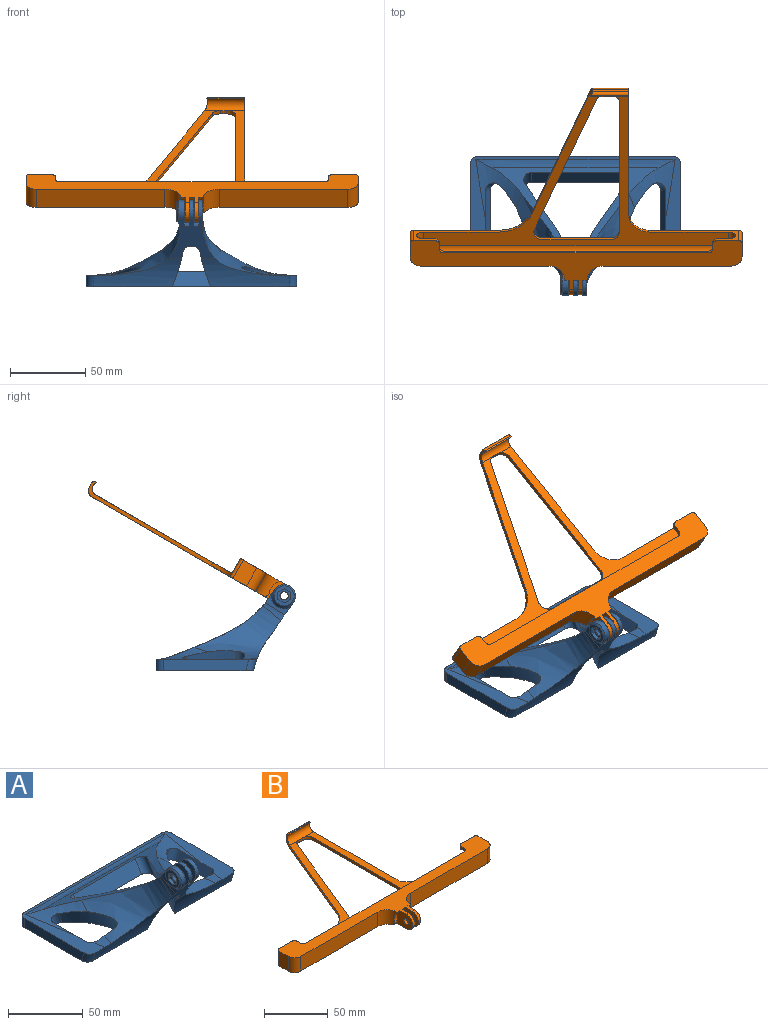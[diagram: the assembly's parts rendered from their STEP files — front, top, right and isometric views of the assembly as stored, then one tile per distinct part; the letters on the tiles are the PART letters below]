
ASSEMBLY  parts=2 mates=1
PART A: 71 faces, bbox 183.3x107.2x68.2 mm
  f0: plane 140.82x67.89mm, normal (0,0,1), area 1387.2mm2, adj f2,f3,f4,f6,f17,f18,f19,f30
  f1: bspline ~80.55x44.88mm, area 1328.5mm2, adj f2,f3,f6,f11,f21,f62,f63,f67
  f2: bspline ~44.93x33.78mm, area 387mm2, adj f0,f1,f21,f55,f63,f64,f65
  f3: bspline ~12.63x10.46mm, area 71.5mm2, adj f0,f1,f6,f66,f67
  f4: bspline ~12.63x10.46mm, area 71.5mm2, adj f0,f20,f30,f58,f59
  f5: plane 142.8x67.8mm, normal (0,0,-1), area 4885.5mm2, adj f6,f17,f18,f19,f30,f38,f39,f40
  f6: cylinder r=49.45mm len=58.6mm, axis (1,0,0), area 654.4mm2, adj f0,f1,f3,f5,f11,f41,f46
  f7: cylinder r=2.75mm len=5.5mm, axis (1,0,0), area 43.2mm2, adj f28,f37
  f8: plane 13.25x13.25mm, normal (-1,0,0), area 78.9mm2, adj f29,f31,f32,f33,f34,f35,f36
  f9: plane 16.64x13.62mm, normal (-1,0,0), area 49.9mm2, adj f11,f12,f29,f69,f70
  f10: cylinder r=2.75mm len=5.5mm, axis (1,0,0), area 47.5mm2, adj f24,f27
  f11: plane 31.78x27.39mm, normal (0,-0.82,-0.57), area 467.4mm2, adj f1,f6,f9,f13,f15,f16,f20,f22
  f12: plane 16.98x9.59mm, normal (0,0.82,0.57), area 122.3mm2, adj f9,f13,f15,f16,f22,f23,f24,f25
  f13: cylinder r=7.62mm len=13.87mm, axis (1,0,0), area 65.9mm2, adj f11,f12,f24,f27
  f14: cylinder r=2.75mm len=5.5mm, axis (1,0,0), area 47.5mm2, adj f16,f25
  f15: cylinder r=7.62mm len=13.87mm, axis (1,0,0), area 89.8mm2, adj f11,f12,f28,f29
  f16: plane 20.33x20.18mm, normal (1,0,0), area 228.9mm2, adj f11,f12,f14,f22,f68,f69
  f17: plane 130x7.5mm, normal (0,1,0), area 975mm2, adj f0,f5,f48,f49
  f18: plane 56.78x7.5mm, normal (-1,0,0), area 418.2mm2, adj f0,f5,f46,f48
  f19: plane 56.78x7.5mm, normal (1,0,0), area 418.2mm2, adj f0,f5,f47,f49
  f20: bspline ~80.55x44.88mm, area 1328.5mm2, adj f4,f11,f21,f30,f54,f56,f57,f58
  f21: bspline ~131.94x66.93mm, area 1213.9mm2, adj f1,f2,f20,f38,f39,f40,f41,f42
  f22: cylinder r=7.62mm len=13.87mm, axis (1,0,0), area 65.9mm2, adj f11,f12,f16,f25
  f23: cylinder r=10mm len=12.49mm, axis (1,0,0), area 60.7mm2, adj f11,f12,f24,f25
  f24: plane 17.63x17.58mm, normal (1,0,0), area 203.6mm2, adj f10,f11,f12,f13,f23
  f25: plane 17.63x17.58mm, normal (-1,0,0), area 203.6mm2, adj f11,f12,f14,f22,f23
  f26: cylinder r=10mm len=12.49mm, axis (-1,0,0), area 60.7mm2, adj f11,f12,f27,f28
  f27: plane 17.63x17.58mm, normal (-1,0,0), area 203.6mm2, adj f10,f11,f12,f13,f26
  f28: plane 17.63x17.58mm, normal (1,0,0), area 203.6mm2, adj f7,f11,f12,f15,f26
  f29: cone r=6.62mm half-angle=45deg, axis (1,0,0), area 93.7mm2, adj f8,f9,f11,f12,f15
  f30: cylinder r=49.45mm len=58.6mm, axis (1,0,0), area 654.4mm2, adj f0,f4,f5,f11,f20,f45,f47
  f31: plane 4.76x2.25mm, normal (0,-1,0), area 10.7mm2, adj f8,f32,f36,f37
  f32: plane 4.13x2.38mm, normal (0,-0.5,0.87), area 10.7mm2, adj f8,f31,f33,f37
  f33: plane 4.13x2.38mm, normal (0,0.5,0.87), area 10.7mm2, adj f8,f32,f34,f37
  f34: plane 4.76x2.25mm, normal (0,1,0), area 10.7mm2, adj f8,f33,f35,f37
  f35: plane 4.13x2.38mm, normal (0,0.5,-0.87), area 10.7mm2, adj f8,f34,f36,f37
  f36: plane 4.13x2.38mm, normal (0,-0.5,-0.87), area 10.7mm2, adj f8,f31,f35,f37
  f37: plane 9.53x8.25mm, normal (-1,0,0), area 35.2mm2, adj f7,f31,f32,f33,f34,f35,f36
  f38: plane 58.76x9.73mm, normal (0,-0.84,0.54), area 681.5mm2, adj f5,f21,f51,f52
  f39: plane 43.2x24.34mm, normal (0.84,0.46,-0.3), area 762.6mm2, adj f5,f21,f41,f52
  f40: plane 43.2x24.34mm, normal (-0.84,0.46,-0.3), area 762.6mm2, adj f5,f21,f45,f51
  f41: cylinder r=57.51mm len=39.06mm, axis (0,0.54,0.84), area 637.8mm2, adj f5,f6,f11,f21,f39,f42
  f42: plane 15.97x10.54mm, normal (0.99,0.11,-0.07), area 18.2mm2, adj f11,f21,f41,f53
  f43: plane 14.35x9.32mm, normal (0,0.84,-0.54), area 24.8mm2, adj f11,f21,f50,f53
  f44: plane 15.97x10.54mm, normal (-0.99,0.11,-0.07), area 18.2mm2, adj f11,f21,f45,f50
  f45: cylinder r=57.51mm len=39.06mm, axis (0,0.54,0.84), area 637.8mm2, adj f5,f11,f21,f30,f40,f44
  f46: torus R=54.45mm, axis (-1,0,0), area 60.3mm2, adj f0,f5,f6,f18
  f47: torus R=54.45mm, axis (-1,0,0), area 60.3mm2, adj f0,f5,f19,f30
  f48: cylinder r=5mm len=7.5mm, axis (0,0,-1), area 58.9mm2, adj f0,f5,f17,f18
  f49: cylinder r=5mm len=7.5mm, axis (0,0,1), area 58.9mm2, adj f0,f5,f17,f19
  f50: cylinder r=5mm len=18.18mm, axis (0,-0.54,-0.84), area 126.2mm2, adj f11,f21,f43,f44
  f51: cylinder r=5mm len=18.13mm, axis (0,-0.54,-0.84), area 142.6mm2, adj f5,f21,f38,f40
  f52: cylinder r=5mm len=18.13mm, axis (0,0.54,0.84), area 142.6mm2, adj f5,f21,f38,f39
  f53: cylinder r=5mm len=18.18mm, axis (0,0.54,0.84), area 126.2mm2, adj f11,f21,f42,f43
  f54: bspline ~56.7x34.87mm, area 387mm2, adj f0,f20,f21,f55,f57,f60,f61
  f55: bspline ~180.45x5.35mm, area 667.4mm2, adj f0,f2,f21,f54
  f56: cylinder r=5mm len=14.93mm, axis (0.38,0,0.92), area 111.6mm2, adj f5,f20,f57,f58
  f57: cylinder r=52.52mm len=34.78mm, axis (0.38,0,0.92), area 480mm2, adj f5,f20,f54,f56,f61
  f58: cylinder r=189.84mm len=20.54mm, axis (0.38,0,0.92), area 153.4mm2, adj f4,f5,f20,f56,f59
  f59: cylinder r=5mm len=11.25mm, axis (0.38,0,0.92), area 64.4mm2, adj f0,f4,f5,f58,f60
  f60: plane 31.15x8.36mm, normal (-0.92,0,0.38), area 247.9mm2, adj f0,f5,f54,f59,f61
  f61: cylinder r=5mm len=13.94mm, axis (0.38,0,0.92), area 102.7mm2, adj f5,f54,f57,f60
  f62: cylinder r=5mm len=14.93mm, axis (-0.38,0,0.92), area 111.6mm2, adj f1,f5,f63,f67
  f63: cylinder r=52.52mm len=34.78mm, axis (-0.38,0,0.92), area 480mm2, adj f1,f2,f5,f62,f64
  f64: cylinder r=5mm len=13.94mm, axis (-0.38,0,0.92), area 102.7mm2, adj f2,f5,f63,f65
  f65: plane 31.15x8.36mm, normal (0.92,0,0.38), area 247.9mm2, adj f0,f2,f5,f64,f66
  f66: cylinder r=5mm len=11.25mm, axis (-0.38,0,0.92), area 64.4mm2, adj f0,f3,f5,f65,f67
  f67: cylinder r=189.84mm len=20.54mm, axis (-0.38,0,0.92), area 153.4mm2, adj f1,f3,f5,f62,f66
  f68: bspline ~17.81x14.16mm, area 55.8mm2, adj f11,f16,f20,f69
  f69: bspline ~18.88x2.42mm, area 48.2mm2, adj f1,f9,f12,f16,f20,f21,f68,f70
  f70: bspline ~17.81x14.16mm, area 55.8mm2, adj f1,f9,f11,f69
PART B: 61 faces, bbox 221x155.5x14 mm
  f0: cylinder r=2.75mm len=5.5mm, axis (1,0,0), area 47.5mm2, adj f51,f54
  f1: cylinder r=7mm len=14mm, axis (1,0,0), area 60.5mm2, adj f6,f7,f48,f55
  f2: cylinder r=2.75mm len=5.5mm, axis (1,0,0), area 47.5mm2, adj f48,f55
  f3: plane 0.25x0.24mm, normal (-1,0,0), area 0mm2, adj f6,f52,f58
  f4: cylinder r=7mm len=14mm, axis (1,0,0), area 60.5mm2, adj f6,f7,f51,f54
  f5: plane 0.25x0.24mm, normal (1,0,0), area 0mm2, adj f6,f50,f59
  f6: plane 221x37.5mm, normal (0,0,1), area 2808.3mm2, adj f1,f3,f4,f5,f8,f20,f21,f22
  f7: plane 221x143.5mm, normal (0,0,-1), area 5593.8mm2, adj f1,f4,f8,f9,f10,f11,f12,f13
  f8: plane 85.38x14mm, normal (0,-1,0), area 1195.3mm2, adj f6,f7,f25,f58
  f9: plane 97x10mm, normal (1,0,0), area 254.8mm2, adj f7,f19,f36,f38,f39,f43,f44,f60
  f10: plane 96.19x39.86mm, normal (-0.92,0.38,0), area 273.6mm2, adj f7,f18,f19,f36,f38,f39,f43,f44
  f11: plane 99x2.5mm, normal (-1,0,0), area 247.5mm2, adj f7,f12,f17,f44
  f12: cylinder r=6mm len=6mm, axis (0,0,-1), area 23.6mm2, adj f7,f11,f13,f44
  f13: plane 45.01x2.5mm, normal (0,1,0), area 112.5mm2, adj f7,f12,f14,f44
  f14: cylinder r=6mm len=8.3mm, axis (0,0,-1), area 29.5mm2, adj f7,f13,f15,f44
  f15: plane 99x41.03mm, normal (0.92,-0.38,0), area 267.9mm2, adj f7,f14,f16,f44
  f16: cylinder r=6mm len=5.54mm, axis (0,0,-1), area 17.7mm2, adj f7,f15,f37,f43,f44
  f17: cylinder r=6mm len=6mm, axis (0,0,-1), area 23.6mm2, adj f7,f11,f37,f43,f44
  f18: cylinder r=24mm len=22.17mm, axis (0,0,1), area 70.7mm2, adj f7,f10,f20,f44
  f19: plane 25.2x0.9mm, normal (0,0,1), area 22.4mm2, adj f9,f10,f38,f43
  f20: plane 57.47x14mm, normal (0,1,0), area 211.1mm2, adj f6,f7,f18,f23,f32,f40,f42,f44
  f21: cylinder r=2mm len=14mm, axis (0,0,1), area 44mm2, adj f6,f7,f22,f28
  f22: plane 59.5x14mm, normal (0,1,0), area 216.2mm2, adj f6,f7,f21,f33,f41,f42,f44,f60
  f23: cylinder r=2mm len=14mm, axis (0,0,1), area 44mm2, adj f6,f7,f20,f24
  f24: plane 14x10.5mm, normal (-1,0,0), area 147mm2, adj f6,f7,f23,f25
  f25: cylinder r=7mm len=14mm, axis (0,0,1), area 153.9mm2, adj f6,f7,f8,f24
  f26: plane 85.38x14mm, normal (0,-1,0), area 1195.3mm2, adj f6,f7,f27,f59
  f27: cylinder r=7mm len=14mm, axis (0,0,1), area 153.9mm2, adj f6,f7,f26,f28
  f28: plane 14x10.5mm, normal (1,0,0), area 147mm2, adj f6,f7,f21,f27
  f29: plane 176x2.5mm, normal (0,1,0), area 440mm2, adj f6,f30,f35,f42
  f30: cylinder r=3mm len=3mm, axis (0,0,-1), area 11.8mm2, adj f6,f29,f31,f42
  f31: plane 3.5x2.5mm, normal (1,0,0), area 8.7mm2, adj f6,f30,f32,f42
  f32: cylinder r=3mm len=3mm, axis (0,0,-1), area 11.8mm2, adj f6,f20,f31,f42
  f33: cylinder r=3mm len=3mm, axis (0,0,-1), area 11.8mm2, adj f6,f22,f34,f42
  f34: plane 3.5x2.5mm, normal (-1,0,0), area 8.7mm2, adj f6,f33,f35,f42
  f35: cylinder r=3mm len=3mm, axis (0,0,-1), area 11.8mm2, adj f6,f29,f34,f42
  f36: plane 24x3mm, normal (0,1,0), area 72mm2, adj f9,f10,f38,f39
  f37: plane 3.98x2.51mm, normal (0,-1,0), area 10mm2, adj f7,f16,f17,f43
  f38: cylinder r=2mm len=24.83mm, axis (1,0,0), area 76.3mm2, adj f9,f10,f19,f36
  f39: cylinder r=5mm len=26.07mm, axis (-1,0,0), area 194.4mm2, adj f7,f9,f10,f36
  f40: cylinder r=4.5mm len=10.5mm, axis (0,1,0), area 148.4mm2, adj f20,f42,f44,f47
  f41: cylinder r=4.5mm len=10.5mm, axis (0,-1,0), area 148.4mm2, adj f22,f42,f44,f45
  f42: plane 203x10.5mm, normal (0,0,-1), area 402.5mm2, adj f20,f22,f29,f30,f31,f32,f33,f34
  f43: cylinder r=4.5mm len=26.59mm, axis (1,0,0), area 259.7mm2, adj f9,f10,f16,f17,f19,f37,f44
  f44: plane 203x115.25mm, normal (0,0,1), area 3210.4mm2, adj f9,f10,f11,f12,f13,f14,f15,f16
  f45: sphere r=4.5mm, area 63.6mm2, adj f41,f46
  f46: cylinder r=4.5mm len=203mm, axis (-1,0,0), area 2869.8mm2, adj f42,f44,f45,f47
  f47: sphere r=4.5mm, area 63.6mm2, adj f40,f46
  f48: plane 19.37x14mm, normal (1,0,0), area 186mm2, adj f1,f2,f6,f7,f49,f50
  f49: cylinder r=3mm len=4.25mm, axis (1,0,0), area 19.5mm2, adj f7,f48,f50,f59
  f50: cylinder r=10mm len=10.08mm, axis (1,0,0), area 34.8mm2, adj f5,f6,f48,f49,f59
  f51: plane 19.37x14mm, normal (-1,0,0), area 186mm2, adj f0,f4,f6,f7,f52,f53
  f52: cylinder r=10mm len=10.08mm, axis (-1,0,0), area 34.8mm2, adj f3,f6,f51,f53,f58
  f53: cylinder r=3mm len=4.25mm, axis (-1,0,0), area 19.5mm2, adj f7,f51,f52,f58
  f54: plane 19.37x14mm, normal (1,0,0), area 186mm2, adj f0,f4,f6,f7,f56,f57
  f55: plane 19.37x14mm, normal (-1,0,0), area 186mm2, adj f1,f2,f6,f7,f56,f57
  f56: cylinder r=3mm len=3.92mm, axis (1,0,0), area 19.8mm2, adj f7,f54,f55,f57
  f57: cylinder r=10mm len=10.08mm, axis (1,0,0), area 38.1mm2, adj f6,f54,f55,f56
  f58: cylinder r=10.62mm len=14mm, axis (0,0,-1), area 203.8mm2, adj f3,f6,f7,f8,f52,f53
  f59: cylinder r=10.62mm len=14mm, axis (0,0,1), area 203.8mm2, adj f5,f6,f7,f26,f49,f50
  f60: cylinder r=14mm len=14mm, axis (0,0,1), area 55mm2, adj f7,f9,f22,f44
PLACE A t=(-16.9,37.37,-30.12)mm
PLACE B rot(axis=(1,0,0),30deg) t=(-16.52,21.39,42.43)mm
MATE revolute B.f57 <-> A.f7  axis (1,0,0) through (-18.27,-51.9,0.12)mm
